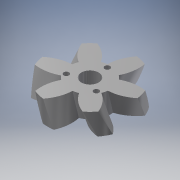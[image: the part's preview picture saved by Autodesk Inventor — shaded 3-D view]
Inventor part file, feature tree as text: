
AUTODESK INVENTOR PART (.ipt)
format: ipt  version: 2017 SP1 (Build 210196100, 196)  size: 304,128 bytes
history: native  units: mm (DEFAULTED — no unit token found)
features: sketch x4, plane x3, other x3, extrude x2, hole x1
ambient origin geometry x8: Origin, YZ Plane, XZ Plane, XY Plane, X Axis, Y Axis, Z Axis, Center Point
bodies: Solid1 (feature_tree)
feature tree (13):
  extrude  "Extrusion1"  Depth=10.0mm TaperAngle=0.0deg
  plane  "Work Plane2"
  plane  "Work Plane8"
  plane  "Work Plane9"
  other  "Engrenage cylindrique"
  extrude  "Extrusion2"  Depth=10.0mm TaperAngle=0.0deg
  hole  "Perçage1"  [1 undecoded]
  sketch  "Sketch1"  dims[d0=38.885336mm d1=10.0mm d2=0.0mm]
  sketch  "Sketch2"  dims[d3=30.066593mm d4=10.0mm d5=0.0mm d16=30.066593mm d17=0.0mm d34=30.0deg d39=0.0mm d41=0.0mm d43=30.066593mm d46=30.066593mm d47=0.0mm d48=0.0mm d49=8.0mm d50=10.0mm d51=0.0mm d52=8.0mm d53=30.0mm d55=360.0deg d57=2.5mm d58=6.0mm d59=4.0mm d60=2.0mm d61=90.0deg d62=8.0mm d63=20.594885mm]
  other  "Srf1"
  sketch  "Esquisse3"
  sketch  "Esquisse4"
  other  "Diamètre primitif"
note: 1 required parameter value undecoded (feature->parameter linkage not recoverable at this tier; creation-order binding heuristic only, values carry confidence <= 0.55)
